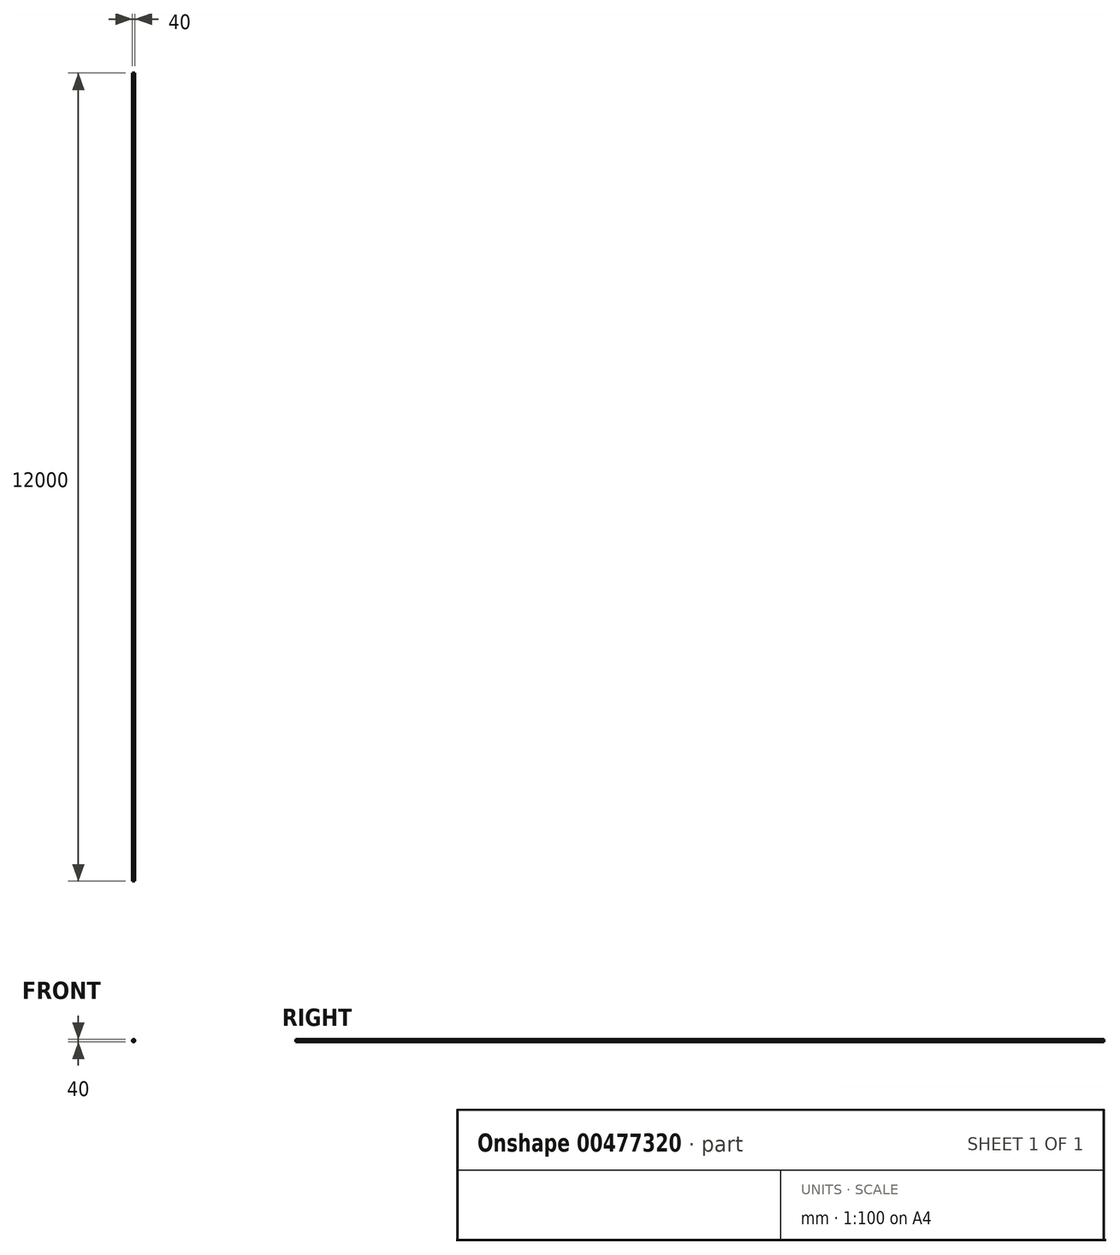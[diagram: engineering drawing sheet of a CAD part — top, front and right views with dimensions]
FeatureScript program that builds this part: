
annotation { "Feature Type Name" : "Feature", "Feature Type Description" : "" }
export const myFeature = defineFeature(function(context is Context, id is Id, definition is map)
    precondition{}
    {
        {
            var Q0;
            Q0=qCreatedBy(makeId("Front.planeOp"),FACE);
            var sketch = newSketch(context, id + "F0", { "sketchPlane" : qUnion([Q0])});
            skCircle(sketch, "E0", {"center": v(0, 0) * mm, "radius": 20 * mm});
            skSolve(sketch);
        }
        {
            var Q0;
            Q0=makeQuery(id+"F0.imprint","IMPRINT",FACE,{"disambiguationData":[TD([[makeQuery(id+"F0.imprint","IMPRINT",EDGE,{"derivedFrom":sQuery(id+"F0.wireOp",EDGE,"E0")}),1.0]])]});
            extrude(context, id + "F1", {"entities" : qUnion([Q0]), "oppositeDirection" : true, "depth" : 12000 * mm});
        }
    });
